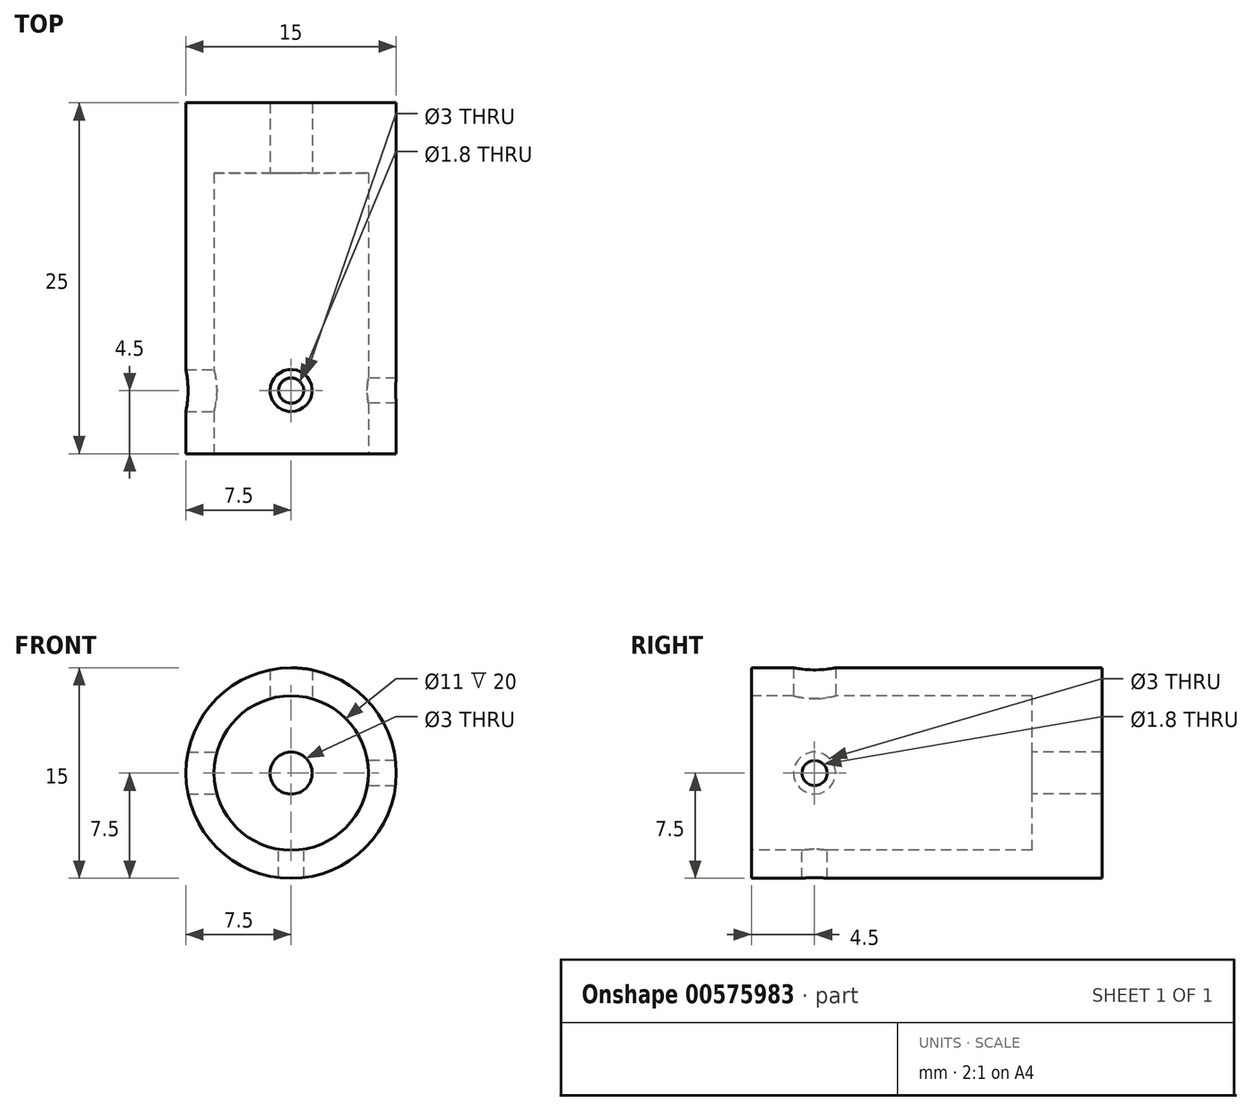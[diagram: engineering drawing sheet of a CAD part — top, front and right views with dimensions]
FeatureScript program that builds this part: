
annotation { "Feature Type Name" : "Feature", "Feature Type Description" : "" }
export const myFeature = defineFeature(function(context is Context, id is Id, definition is map)
    precondition{}
    {
        {
            var Q0;
            Q0=qCreatedBy(makeId("Front.planeOp"),FACE);
            var sketch = newSketch(context, id + "F0", { "sketchPlane" : qUnion([Q0])});
            skCircle(sketch, "E0", {"center": v(0, 0) * mm, "radius": 7.5 * mm});
            skSolve(sketch);
        }
        {
            var Q0;
            Q0 = qSketchRegion(id + "F0", true);
            extrude(context, id + "F1", {"entities" : qUnion([Q0]), "depth" : 25 * mm, "offsetDistance" : 25 * mm});
        }
        {
            var Q0;
            Q0=makeQuery(id+"F1.opExtrude","CAP_FACE",FACE,{"disambiguationData":[OSD([sQuery(id+"F0.wireOp",EDGE,"E0")])],"isStart":false});
            var sketch = newSketch(context, id + "F2", { "sketchPlane" : qUnion([Q0])});
            skCircle(sketch, "E1", {"center": v(0, 0) * mm, "radius": 5.5 * mm});
            skCircle(sketch, "E2.0.0", {"center": v(0, 0) * mm, "radius": 7.5 * mm, "construction": true});
            skSolve(sketch);
        }
        {
            var Q0;
            Q0=makeQuery(id+"F2.imprint","IMPRINT",FACE,{"disambiguationData":[TD([[makeQuery(id+"F2.imprint","IMPRINT",EDGE,{"derivedFrom":sQuery(id+"F2.wireOp",EDGE,"E1")}),1.0]])]});
            extrude(context, id + "F3", {"entities" : qUnion([Q0]), "operationType" : NewBodyOperationType.REMOVE, "oppositeDirection" : true, "depth" : 20 * mm, "offsetDistance" : 25 * mm});
        }
        {
            var Q0;
            Q0=makeQuery(id+"F3.boolean.opBoolean","COPY",FACE,{"derivedFrom":makeQuery(id+"F3.opExtrude","CAP_FACE",FACE,{"disambiguationData":[OSD([sQuery(id+"F2.wireOp",EDGE,"E1")])],"isStart":false})});
            var sketch = newSketch(context, id + "F4", { "sketchPlane" : qUnion([Q0])});
            skCircle(sketch, "E3", {"center": v(0, 0) * mm, "radius": 1.5 * mm});
            skSolve(sketch);
        }
        {
            var Q0;
            Q0 = qSketchRegion(id + "F4", true);
            var Q1;
            Q1=makeQuery(id+"F1.opExtrude","CAP_FACE",FACE,{"disambiguationData":[OSD([sQuery(id+"F0.wireOp",EDGE,"E0")])],"isStart":true});
            extrude(context, id + "F5", {"entities" : qUnion([Q0]), "operationType" : NewBodyOperationType.REMOVE, "endBound" : BoundingType.UP_TO_SURFACE, "oppositeDirection" : true, "depth" : 25 * mm, "endBoundEntityFace" : qUnion([Q1]), "offsetDistance" : 25 * mm});
        }
        {
            var Q0;
            Q0=qCreatedBy(makeId("Top.planeOp"),FACE);
            var sketch = newSketch(context, id + "F6", { "sketchPlane" : qUnion([Q0])});
            skCircle(sketch, "E4", {"center": v(0, -20.5) * mm, "radius": 1.5 * mm});
            skLineSegment(sketch, "E5.0", {"start": v(7.5, -25) * mm, "end": v(-7.5, -25) * mm, "construction": true});
            skSolve(sketch);
        }
        {
            var Q0;
            Q0 = qSketchRegion(id + "F6", true);
            extrude(context, id + "F7", {"entities" : qUnion([Q0]), "operationType" : NewBodyOperationType.REMOVE, "endBound" : BoundingType.THROUGH_ALL, "depth" : 25 * mm, "offsetDistance" : 25 * mm});
        }
        {
            var Q0;
            Q0=qCreatedBy(makeId("Top.planeOp"),FACE);
            var sketch = newSketch(context, id + "F8", { "sketchPlane" : qUnion([Q0])});
            skCircle(sketch, "E6", {"center": v(0, -20.5) * mm, "radius": 0.9 * mm});
            skCircle(sketch, "E7.0", {"center": v(0, -20.5) * mm, "radius": 1.5 * mm, "construction": true});
            skSolve(sketch);
        }
        {
            var Q0;
            Q0 = qSketchRegion(id + "F8", true);
            extrude(context, id + "F9", {"entities" : qUnion([Q0]), "operationType" : NewBodyOperationType.REMOVE, "endBound" : BoundingType.THROUGH_ALL, "oppositeDirection" : true, "depth" : 25 * mm, "offsetDistance" : 25 * mm});
        }
        {
            var Q0;
            Q0=qCreatedBy(makeId("Right.planeOp"),FACE);
            var sketch = newSketch(context, id + "F10", { "sketchPlane" : qUnion([Q0])});
            skCircle(sketch, "E8", {"center": v(-20.5, 0) * mm, "radius": 1.5 * mm});
            skSolve(sketch);
        }
        {
            var Q0;
            Q0 = qSketchRegion(id + "F10", true);
            extrude(context, id + "F11", {"entities" : qUnion([Q0]), "operationType" : NewBodyOperationType.REMOVE, "endBound" : BoundingType.THROUGH_ALL, "oppositeDirection" : true, "depth" : 25 * mm, "offsetDistance" : 25 * mm});
        }
        {
            var Q0;
            Q0=qCreatedBy(makeId("Right.planeOp"),FACE);
            var sketch = newSketch(context, id + "F12", { "sketchPlane" : qUnion([Q0])});
            skCircle(sketch, "E9.0", {"center": v(-20.5, 0) * mm, "radius": 1.5 * mm, "construction": true});
            skCircle(sketch, "E10", {"center": v(-20.5, 0) * mm, "radius": 0.9 * mm});
            skSolve(sketch);
        }
        {
            var Q0;
            Q0 = qSketchRegion(id + "F12", true);
            extrude(context, id + "F13", {"entities" : qUnion([Q0]), "operationType" : NewBodyOperationType.REMOVE, "endBound" : BoundingType.THROUGH_ALL, "depth" : 25 * mm, "offsetDistance" : 25 * mm});
        }
    });
